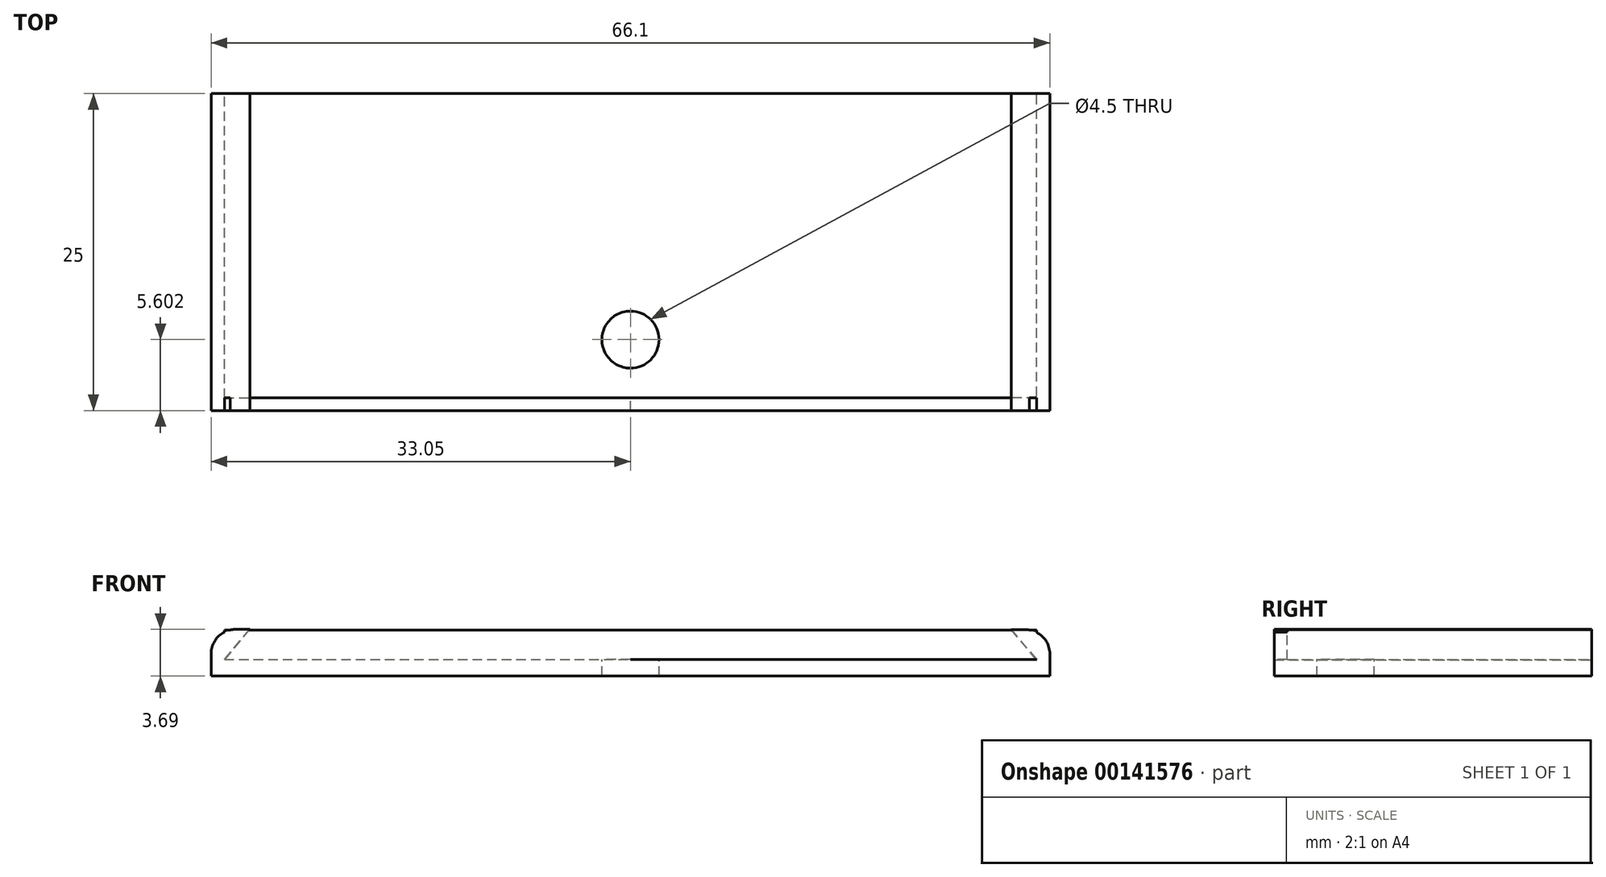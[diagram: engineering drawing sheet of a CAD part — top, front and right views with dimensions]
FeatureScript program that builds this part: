
annotation { "Feature Type Name" : "Feature", "Feature Type Description" : "" }
export const myFeature = defineFeature(function(context is Context, id is Id, definition is map)
    precondition{}
    {
        {
            var Q0;
            Q0=qCreatedBy(makeId("Front.planeOp"),FACE);
            var sketch = newSketch(context, id + "F0", { "sketchPlane" : qUnion([Q0])});
            skLineSegment(sketch, "E0.bottom", {"start": v(0, -0.65) * mm, "end": v(-33.05, -0.65) * mm});
            skLineSegment(sketch, "E0.top", {"start": v(0, 0.65) * mm, "end": v(-32, 0.65) * mm});
            skLineSegment(sketch, "E0.right", {"start": v(-33.05, -0.65) * mm, "end": v(-33.05, 0.65) * mm});
            skPoint(sketch, "E0.middle", {"position": v(0, 0) * mm});
            skLineSegment(sketch, "E1", {"start": v(-33.05, 0.65) * mm, "end": v(-33.05, 1.1) * mm});
            skLineSegment(sketch, "E2", {"start": v(-31.12, 3.02) * mm, "end": v(-30, 3.02) * mm});
            skLineSegment(sketch, "E3", {"start": v(-30, 3.02) * mm, "end": v(-32, 0.65) * mm});
            skLineSegment(sketch, "E4", {"start": v(0, 0.65) * mm, "end": v(0, -0.65) * mm});
            skPoint(sketch, "E0.left.end.orphan", {"position": v(33.05, 0.65) * mm});
            skPoint(sketch, "E0.left.start.orphan", {"position": v(33.05, -0.65) * mm});
            skPoint(sketch, "E5.visualSharp", {"position": v(-33.05, 3.02) * mm});
            skArc(sketch, "E5.filletArc", {"start": v(-31.12, 3.02) * mm, "mid": v(-32.49, 2.46) * mm, "end": v(-33.05, 1.1) * mm});
            skLineSegment(sketch, "E6.MirrorCS", {"start": v(33.05, 0.63) * mm, "end": v(33.05, 1.07) * mm});
            skLineSegment(sketch, "E7.MirrorCS", {"start": v(0, -0.65) * mm, "end": v(33.05, -0.67) * mm});
            skPoint(sketch, "E8.MirrorP", {"position": v(33.05, 3) * mm});
            skLineSegment(sketch, "E9.MirrorCS", {"start": v(0, 0.65) * mm, "end": v(32, 0.63) * mm});
            skLineSegment(sketch, "E10.MirrorCS", {"start": v(33.05, -0.67) * mm, "end": v(33.05, 0.63) * mm});
            skLineSegment(sketch, "E11.MirrorCS", {"start": v(31.13, 3) * mm, "end": v(30.01, 3) * mm});
            skLineSegment(sketch, "E12.MirrorCS", {"start": v(30.01, 3) * mm, "end": v(32, 0.63) * mm});
            skArc(sketch, "E13.MirrorCS", {"start": v(31.13, 3) * mm, "mid": v(32.49, 2.43) * mm, "end": v(33.05, 1.07) * mm});
            skSolve(sketch);
        }
        {
            var Q0;
            Q0=qSketchRegion(id+"F0",true);
            extrude(context, id + "F1", {"entities" : qUnion([Q0]), "depth" : 25 * mm});
        }
        {
            var Q0;
            Q0=makeQuery(id+"F1.opExtrude","SWEPT_FACE",FACE,{"disambiguationData":[OSD([sQuery(id+"F0.wireOp",EDGE,"E9.MirrorCS"),sQuery(id+"F0.wireOp",EDGE,"E0.top")])]});
            var sketch = newSketch(context, id + "F2", { "sketchPlane" : qUnion([Q0])});
            skCircle(sketch, "E14", {"center": v(0, -19.4) * mm, "radius": 2.25 * mm});
            skSolve(sketch);
        }
        {
            var Q0;
            Q0=qSketchRegion(id+"F2",true);
            extrude(context, id + "F3", {"entities" : qUnion([Q0]), "operationType" : NewBodyOperationType.REMOVE, "oppositeDirection" : true, "depth" : 25 * mm});
        }
        {
            var Q0;
            Q0=makeQuery(id+"F1.opExtrude","SWEPT_FACE",FACE,{"disambiguationData":[OSD([sQuery(id+"F0.wireOp",EDGE,"E9.MirrorCS"),sQuery(id+"F0.wireOp",EDGE,"E0.top")])]});
            var sketch = newSketch(context, id + "F4", { "sketchPlane" : qUnion([Q0])});
            skLineSegment(sketch, "E15.bottom", {"start": v(-32, -25) * mm, "end": v(32, -25) * mm});
            skLineSegment(sketch, "E15.top", {"start": v(-32, -24) * mm, "end": v(32, -24) * mm});
            skLineSegment(sketch, "E15.left", {"start": v(-32, -25) * mm, "end": v(-32, -24) * mm});
            skLineSegment(sketch, "E15.right", {"start": v(32, -25) * mm, "end": v(32, -24) * mm});
            skSolve(sketch);
        }
        {
            var Q0;
            Q0=qSketchRegion(id+"F4",true);
            extrude(context, id + "F5", {"entities" : qUnion([Q0]), "operationType" : NewBodyOperationType.ADD, "depth" : 2.32 * mm});
        }
    });
